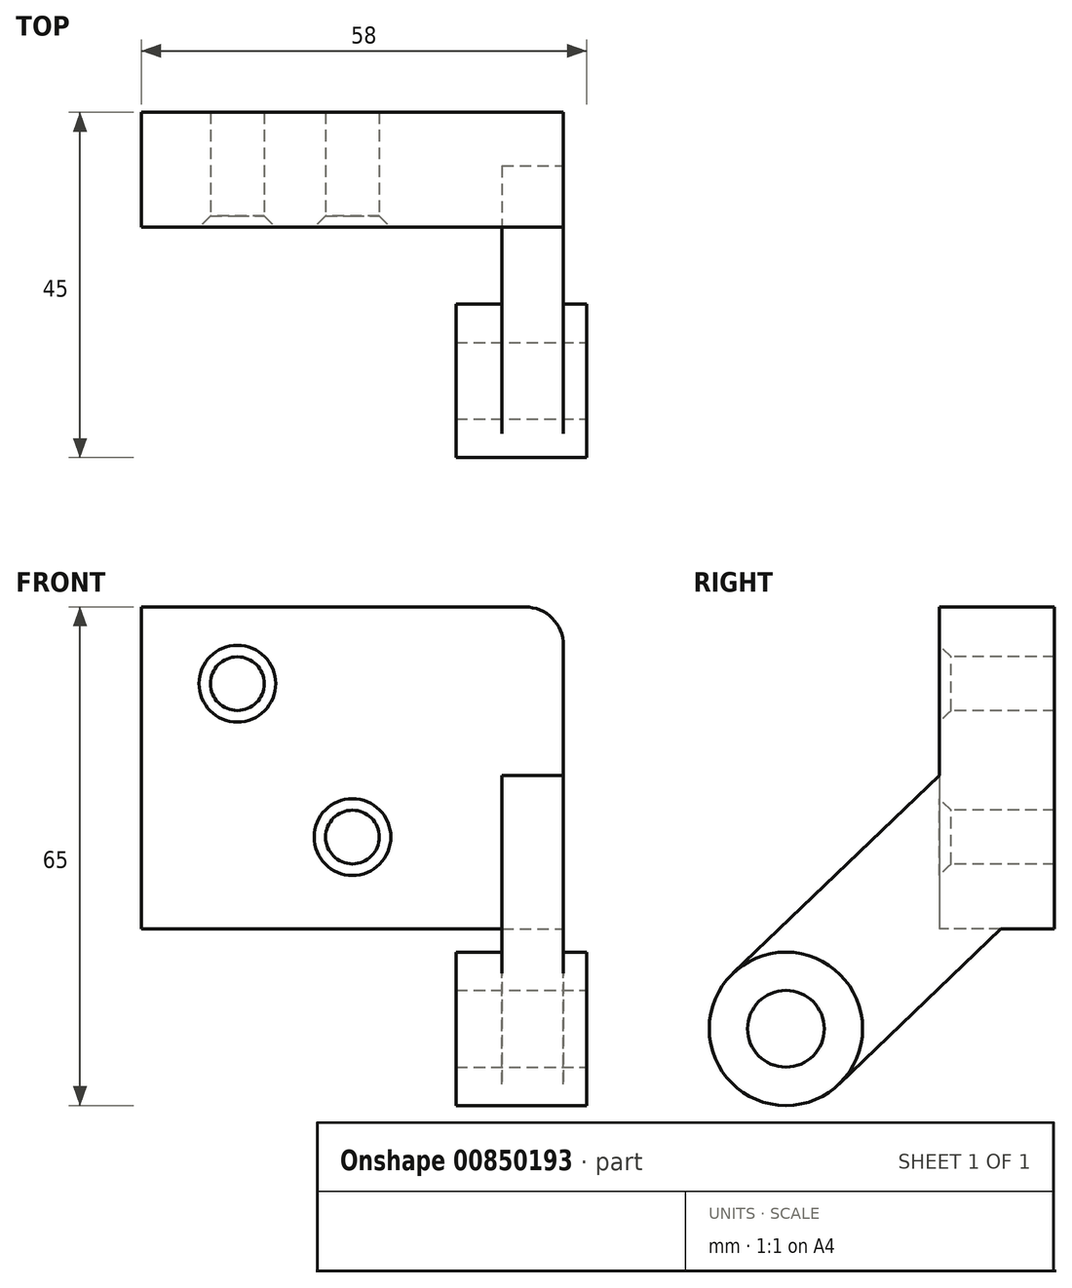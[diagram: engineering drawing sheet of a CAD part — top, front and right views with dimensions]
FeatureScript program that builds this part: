
annotation { "Feature Type Name" : "Feature", "Feature Type Description" : "" }
export const myFeature = defineFeature(function(context is Context, id is Id, definition is map)
    precondition{}
    {
        {
            var Q0;
            Q0=qCreatedBy(makeId("Front.planeOp"),FACE);
            var sketch = newSketch(context, id + "F0", { "sketchPlane" : qUnion([Q0])});
            skLineSegment(sketch, "E0.bottom", {"start": v(-27.5, 0) * mm, "end": v(27.5, 0) * mm});
            skLineSegment(sketch, "E0.top", {"start": v(-27.5, -42) * mm, "end": v(27.5, -42) * mm});
            skLineSegment(sketch, "E0.left", {"start": v(-27.5, 0) * mm, "end": v(-27.5, -42) * mm});
            skLineSegment(sketch, "E0.right", {"start": v(27.5, 0) * mm, "end": v(27.5, -42) * mm});
            skSolve(sketch);
        }
        {
            var Q0;
            Q0=makeQuery(id+"F0.imprint","IMPRINT",FACE,{"disambiguationData":[TD([[makeQuery(id+"F0.imprint","IMPRINT",EDGE,{"derivedFrom":sQuery(id+"F0.wireOp",EDGE,"E0.bottom")}),-1.0]])]});
            var Q1;
            Q1=sQuery(id+"F0.wireOp",EDGE,"E0.right");
            extrude(context, id + "F1", {"entities" : qUnion([Q0]), "surfaceEntities" : qUnion([Q1]), "oppositeDirection" : true, "depth" : 15 * mm, "offsetDistance" : 25 * mm});
        }
        {
            var Q0;
            Q0=makeQuery(id+"F1.opExtrude","SWEPT_FACE",FACE,{"disambiguationData":[OSD([sQuery(id+"F0.wireOp",EDGE,"E0.right")])]});
            var sketch = newSketch(context, id + "F2", { "sketchPlane" : qUnion([Q0])});
            skLineSegment(sketch, "E1", {"start": v(0, -21.96) * mm, "end": v(-26.92, -47.78) * mm});
            skLineSegment(sketch, "E2", {"start": v(8, -42) * mm, "end": v(-13.08, -62.22) * mm});
            skLineSegment(sketch, "E3", {"start": v(-26.92, -47.78) * mm, "end": v(-13.08, -62.22) * mm});
            skCircle(sketch, "E4", {"center": v(-20, -55) * mm, "radius": 10 * mm});
            skCircle(sketch, "E5", {"center": v(-20, -55) * mm, "radius": 5 * mm});
            skSolve(sketch);
        }
        {
            var Q0;
            {var subQ7=sQuery(id+"F2.wireOp",EDGE,"E1");Q0=makeQuery(id+"F2.imprint","IMPRINT",FACE,{"disambiguationData":[TD([[makeQuery(id+"F2.imprint","IMPRINT",EDGE,{"derivedFrom":subQ7}),1.0]])]});}
            extrude(context, id + "F3", {"entities" : qUnion([Q0]), "operationType" : NewBodyOperationType.ADD, "oppositeDirection" : true, "depth" : 8 * mm, "offsetDistance" : 25 * mm});
        }
        {
            var Q0;
            {var subQ1=sQuery(id+"F2.wireOp",EDGE,"E3");var subQ3=sQuery(id+"F2.wireOp",EDGE,"E5");var subQ4=makeQuery(id+"F2.imprint","INTERSECT",VERTEX,{"disambiguationData":[OD(0.0)],"derivedFrom":[subQ1,subQ3]});Q0=makeQuery(id+"F2.imprint","IMPRINT",FACE,{"disambiguationData":[TD([[makeQuery(id+"F2.imprint","IMPRINT",EDGE,{"disambiguationData":[TD([[subQ4,1.0]])],"derivedFrom":subQ3}),-1.0]])]});}
            var Q1;
            {var subQ1=sQuery(id+"F2.wireOp",EDGE,"E3");var subQ3=sQuery(id+"F2.wireOp",EDGE,"E5");var subQ4=makeQuery(id+"F2.imprint","INTERSECT",VERTEX,{"disambiguationData":[OD(0.0)],"derivedFrom":[subQ1,subQ3]});Q1=makeQuery(id+"F2.imprint","IMPRINT",FACE,{"disambiguationData":[TD([[makeQuery(id+"F2.imprint","IMPRINT",EDGE,{"disambiguationData":[TD([[subQ4,-1.0]])],"derivedFrom":subQ3}),-1.0]])]});}
            extrude(context, id + "F4", {"entities" : qUnion([Q0, Q1]), "operationType" : NewBodyOperationType.ADD, "oppositeDirection" : true, "depth" : 14 * mm, "offsetDistance" : 25 * mm, "hasSecondDirection" : true, "secondDirectionOppositeDirection" : false, "secondDirectionDepth" : 3 * mm});
        }
        {
            var Q0;
            Q0=makeQuery(id+"F1.opExtrude","CAP_FACE",FACE,{"disambiguationData":[OSD([sQuery(id+"F0.wireOp",EDGE,"E0.bottom"),sQuery(id+"F0.wireOp",EDGE,"E0.top"),sQuery(id+"F0.wireOp",EDGE,"E0.left"),sQuery(id+"F0.wireOp",EDGE,"E0.right")])],"isStart":true});
            var sketch = newSketch(context, id + "F5", { "sketchPlane" : qUnion([Q0])});
            skPoint(sketch, "E6", {"position": v(-15, -10) * mm});
            skPoint(sketch, "E7", {"position": v(15, -10) * mm});
            skPoint(sketch, "E8", {"position": v(0, -30) * mm});
            skSolve(sketch);
        }
        {
            var Q0;
            Q0=sQuery(id+"F5.wireOp",VERTEX,"E6");
            var Q1;
            Q1=sQuery(id+"F5.wireOp",VERTEX,"E8");
            var Q2;
            Q2=makeQuery(id+"F1.opExtrude","SWEPT_BODY",BODY,{"disambiguationData":[OSD([sQuery(id+"F0.wireOp",EDGE,"E0.bottom"),sQuery(id+"F0.wireOp",EDGE,"E0.top"),sQuery(id+"F0.wireOp",EDGE,"E0.left"),sQuery(id+"F0.wireOp",EDGE,"E0.right")])]});
            hole(context, id + "F6", {"style" : HoleStyle.C_SINK, "endStyle" : HoleEndStyle.THROUGH, "holeDiameter" : 7 * mm, "cSinkDiameter" : 10 * mm, "cSinkAngle" : 90 * degree, "majorDiameter" : 5 * mm, "isTappedThrough" : true, "tappedDepth" : 12 * mm, "tapClearance" : 3, "locations" : qUnion([Q0, Q1]), "scope" : qUnion([Q2])});
        }
        {
            var Q0;
            Q0=makeQuery(id+"F1.opExtrude","SWEPT_EDGE",EDGE,{"disambiguationData":[OSD([sQuery(id+"F0.wireOp",EDGE,"E0.bottom"),sQuery(id+"F0.wireOp",EDGE,"E0.right")])]});
            fillet(context, id + "F7", {"entities" : qUnion([Q0]), "radius" : 5 * mm, "tangentPropagation" : true, "allowEdgeOverflow" : false});
        }
    });
